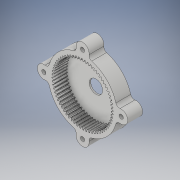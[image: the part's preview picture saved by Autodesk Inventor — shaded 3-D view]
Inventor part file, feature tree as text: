
AUTODESK INVENTOR PART (.ipt)
format: ipt  version: 2019 (Build 230136000, 136)  size: 2,408,448 bytes
history: native  units: in
note: dims shown in document units (in); Inventor stores cm internally (conversion verified against a paired STEP export)
features: sketch x9, extrude x8, projected_geometry x5, plane x2, fillet x1
ambient origin geometry x8: Origin, YZ Plane, XZ Plane, XY Plane, X Axis, Y Axis, Z Axis, Center Point
bodies: Solid1 (feature_tree)
feature tree (25):
  plane  "Work Plane2"
  plane  "Work Plane1"
  extrude  "Extrusion2"  Depth=2.2548in
  extrude  "Extrusion3"  Depth=0.19in TaperAngle=0.0deg
  extrude  "Extrusion4"  Depth=0.05in TaperAngle=0.0deg
  extrude  "Extrusion5"  Depth=0.05in TaperAngle=0.0deg
  extrude  "Extrusion6"  Depth=0.45in TaperAngle=0.0deg
  extrude  "Extrusion7"  Depth=0.14in
  extrude  "Extrusion8"  Depth=0.7874in TaperAngle=0.0deg
  extrude  "Extrusion9"  Depth=1.5748in TaperAngle=0.0deg
  sketch  "Sketch10"  dims[d37=0.4in d38=0.0in d39=0.125in]
  fillet  "Fillet1"  [1 undecoded]
  sketch  "Sketch2"  dims[d3=0.19in d4=0.0in d5=2.2548in]
  projected_geometry  "Projected Loop2"
  sketch  "Sketch3"  dims[d7=0.2in d8=0.19in d9=0.0in]
  sketch  "Sketch4"  dims[d10=0.01in d11=0.0in d12=0.05in d13=0.0in]
  projected_geometry  "Projected Loop3"
  sketch  "Sketch5"  dims[d14=0.05in d15=0.0in d16=0.2in d17=0.0in]
  projected_geometry  "Projected Loop4"
  sketch  "Sketch6"  dims[d18=0.45in d19=0.2in d20=0.0in]
  sketch  "Sketch7"  dims[d21=0.15in d22=0.14in]
  projected_geometry  "Projected Loop5"
  sketch  "Sketch8"  dims[d23=1.3in d24=0.7874in d26=0.0in]
  sketch  "Sketch9"  dims[d28=1.5748in d30=0.0in d32=1.5748in d34=0.0in d36=45.0deg]
  projected_geometry  "Projected Loop6"
note: 1 required parameter value undecoded (feature->parameter linkage not recoverable at this tier; creation-order binding heuristic only, values carry confidence <= 0.55)
